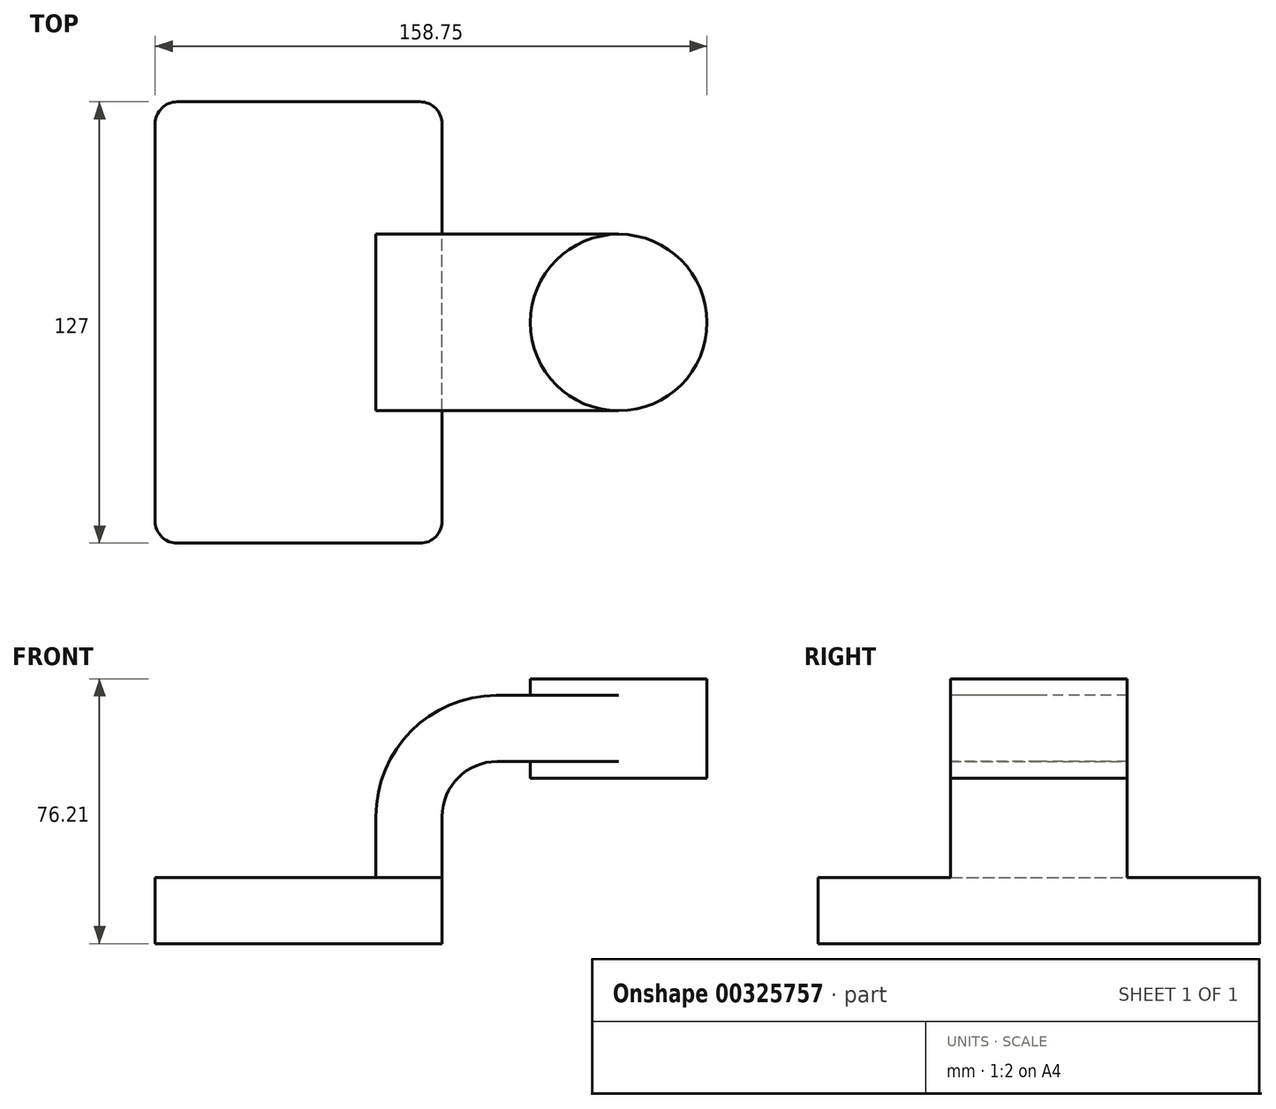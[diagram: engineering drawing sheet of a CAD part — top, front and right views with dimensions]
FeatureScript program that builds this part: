
annotation { "Feature Type Name" : "Feature", "Feature Type Description" : "" }
export const myFeature = defineFeature(function(context is Context, id is Id, definition is map)
    precondition{}
    {
        {
            var Q0;
            Q0=qCreatedBy(makeId("Front.planeOp"),FACE);
            var sketch = newSketch(context, id + "F0", { "sketchPlane" : qUnion([Q0])});
            skLineSegment(sketch, "E0.bottom", {"start": v(41.27, 9.53) * mm, "end": v(-41.28, 9.53) * mm});
            skLineSegment(sketch, "E0.top", {"start": v(41.28, -9.52) * mm, "end": v(-41.27, -9.52) * mm});
            skLineSegment(sketch, "E0.left", {"start": v(41.28, 9.53) * mm, "end": v(41.28, -9.52) * mm});
            skLineSegment(sketch, "E0.right", {"start": v(-41.28, 9.53) * mm, "end": v(-41.27, -9.52) * mm});
            skPoint(sketch, "E0.middle", {"position": v(0, 0) * mm});
            skLineSegment(sketch, "E1.bottom", {"start": v(117.47, 38.1) * mm, "end": v(66.67, 38.1) * mm});
            skLineSegment(sketch, "E1.top", {"start": v(117.47, 66.68) * mm, "end": v(66.67, 66.68) * mm});
            skLineSegment(sketch, "E1.left", {"start": v(117.47, 38.1) * mm, "end": v(117.47, 66.68) * mm});
            skLineSegment(sketch, "E1.right", {"start": v(66.67, 38.1) * mm, "end": v(66.67, 66.68) * mm});
            skPoint(sketch, "E1.middle", {"position": v(92.07, 52.39) * mm});
            skLineSegment(sketch, "E2", {"start": v(41.27, 9.53) * mm, "end": v(41.27, 27) * mm});
            skArc(sketch, "E3", {"start": v(41.27, 27) * mm, "mid": v(45.92, 38.23) * mm, "end": v(57.15, 42.88) * mm});
            skLineSegment(sketch, "E4", {"start": v(57.15, 42.88) * mm, "end": v(92.07, 42.88) * mm});
            skLineSegment(sketch, "E5.0", {"start": v(57.15, 61.93) * mm, "end": v(92.07, 61.93) * mm});
            skArc(sketch, "E5.1", {"start": v(22.22, 27) * mm, "mid": v(32.45, 51.7) * mm, "end": v(57.15, 61.93) * mm});
            skLineSegment(sketch, "E5.2", {"start": v(22.22, 9.53) * mm, "end": v(22.22, 27) * mm});
            skLineSegment(sketch, "E6", {"start": v(92.07, 38.1) * mm, "end": v(92.07, 66.68) * mm});
            skFitSpline(sketch, "E7", {"points": [v(-41.28, 9.53) * mm, v(57.15, 61.93) * mm], "startDerivative": vector(5.9, 42.12) * mm, "endDerivative": vector(238.27, 0.72) * mm});
            skSolve(sketch);
        }
        {
            var Q0;
            Q0=makeQuery(id+"F0.imprint","IMPRINT",FACE,{"disambiguationData":[TD([[makeQuery(id+"F0.imprint","IMPRINT",EDGE,{"derivedFrom":sQuery(id+"F0.wireOp",EDGE,"E0.top")}),-1.0]])]});
            extrude(context, id + "F1", {"entities" : qUnion([Q0]), "endBound" : BoundingType.SYMMETRIC, "depth" : 127 * mm});
        }
        {
            var Q0;
            {var subQ1=sQuery(id+"F0.wireOp",EDGE,"E2");Q0=makeQuery(id+"F0.imprint","IMPRINT",FACE,{"disambiguationData":[TD([[makeQuery(id+"F0.imprint","IMPRINT",EDGE,{"derivedFrom":subQ1}),1.0]])]});}
            var Q1;
            {var subQ0=sQuery(id+"F0.wireOp",EDGE,"E4");var subQ1=sQuery(id+"F0.wireOp",EDGE,"E1.right");var subQ2=makeQuery(id+"F0.imprint","INTERSECT",VERTEX,{"derivedFrom":[subQ1,subQ0]});Q1=makeQuery(id+"F0.imprint","IMPRINT",FACE,{"disambiguationData":[TD([[makeQuery(id+"F0.imprint","IMPRINT",EDGE,{"disambiguationData":[TD([[subQ2,-1.0]])],"derivedFrom":subQ1}),-1.0]])]});}
            extrude(context, id + "F2", {"entities" : qUnion([Q0, Q1]), "operationType" : NewBodyOperationType.ADD, "endBound" : BoundingType.SYMMETRIC, "depth" : 50.8 * mm});
        }
        {
            var Q0;
            Q0=makeQuery(id+"F0.imprint","IMPRINT",FACE,{"disambiguationData":[TD([[makeQuery(id+"F0.imprint","IMPRINT",EDGE,{"derivedFrom":sQuery(id+"F0.wireOp",EDGE,"E0.top")}),-1.0]])]});
            var Q1;
            {var subQ1=sQuery(id+"F0.wireOp",EDGE,"E2");Q1=makeQuery(id+"F0.imprint","IMPRINT",FACE,{"disambiguationData":[TD([[makeQuery(id+"F0.imprint","IMPRINT",EDGE,{"derivedFrom":subQ1}),1.0]])]});}
            var Q2;
            {var subQ0=sQuery(id+"F0.wireOp",EDGE,"E4");var subQ1=sQuery(id+"F0.wireOp",EDGE,"E1.right");var subQ2=makeQuery(id+"F0.imprint","INTERSECT",VERTEX,{"derivedFrom":[subQ1,subQ0]});Q2=makeQuery(id+"F0.imprint","IMPRINT",FACE,{"disambiguationData":[TD([[makeQuery(id+"F0.imprint","IMPRINT",EDGE,{"disambiguationData":[TD([[subQ2,-1.0]])],"derivedFrom":subQ1}),-1.0]])]});}
            var Q3;
            Q3=makeQuery(id+"F0.imprint","IMPRINT",FACE,{"disambiguationData":[TD([[makeQuery(id+"F0.imprint","IMPRINT",EDGE,{"derivedFrom":sQuery(id+"F0.wireOp",EDGE,"E5.1")}),1.0]])]});
            extrude(context, id + "F3", {"entities" : qUnion([Q0, Q1, Q2, Q3]), "operationType" : NewBodyOperationType.ADD, "endBound" : BoundingType.SYMMETRIC, "depth" : 15.88 * mm});
        }
        {
            var Q0;
            {var subQ4=sQuery(id+"F0.wireOp",EDGE,"E1.left");Q0=makeQuery(id+"F0.imprint","IMPRINT",FACE,{"disambiguationData":[TD([[makeQuery(id+"F0.imprint","IMPRINT",EDGE,{"derivedFrom":subQ4}),1.0]])]});}
            var Q1;
            Q1=sQuery(id+"F0.wireOp",EDGE,"E6");
            revolve(context, id + "F4", {"operationType" : NewBodyOperationType.ADD, "entities" : qUnion([Q0]), "axis" : qUnion([Q1]), "revolveType" : RevolveType.FULL});
        }
        {
            var Q0;
            Q0=makeQuery(id+"F1.opExtrude","CAP_EDGE",EDGE,{"disambiguationData":[OSD([sQuery(id+"F0.wireOp",EDGE,"E0.right")])],"isStart":false});
            var Q1;
            Q1=makeQuery(id+"F1.opExtrude","CAP_EDGE",EDGE,{"disambiguationData":[OSD([sQuery(id+"F0.wireOp",EDGE,"E0.left")])],"isStart":false});
            var Q2;
            Q2=makeQuery(id+"F1.opExtrude","CAP_EDGE",EDGE,{"disambiguationData":[OSD([sQuery(id+"F0.wireOp",EDGE,"E0.left")])],"isStart":true});
            var Q3;
            Q3=makeQuery(id+"F1.opExtrude","CAP_EDGE",EDGE,{"disambiguationData":[OSD([sQuery(id+"F0.wireOp",EDGE,"E0.right")])],"isStart":true});
            fillet(context, id + "F5", {"entities" : qUnion([Q0, Q1, Q2, Q3]), "radius" : 6.35 * mm, "tangentPropagation" : true, "allowEdgeOverflow" : false});
        }
    });
